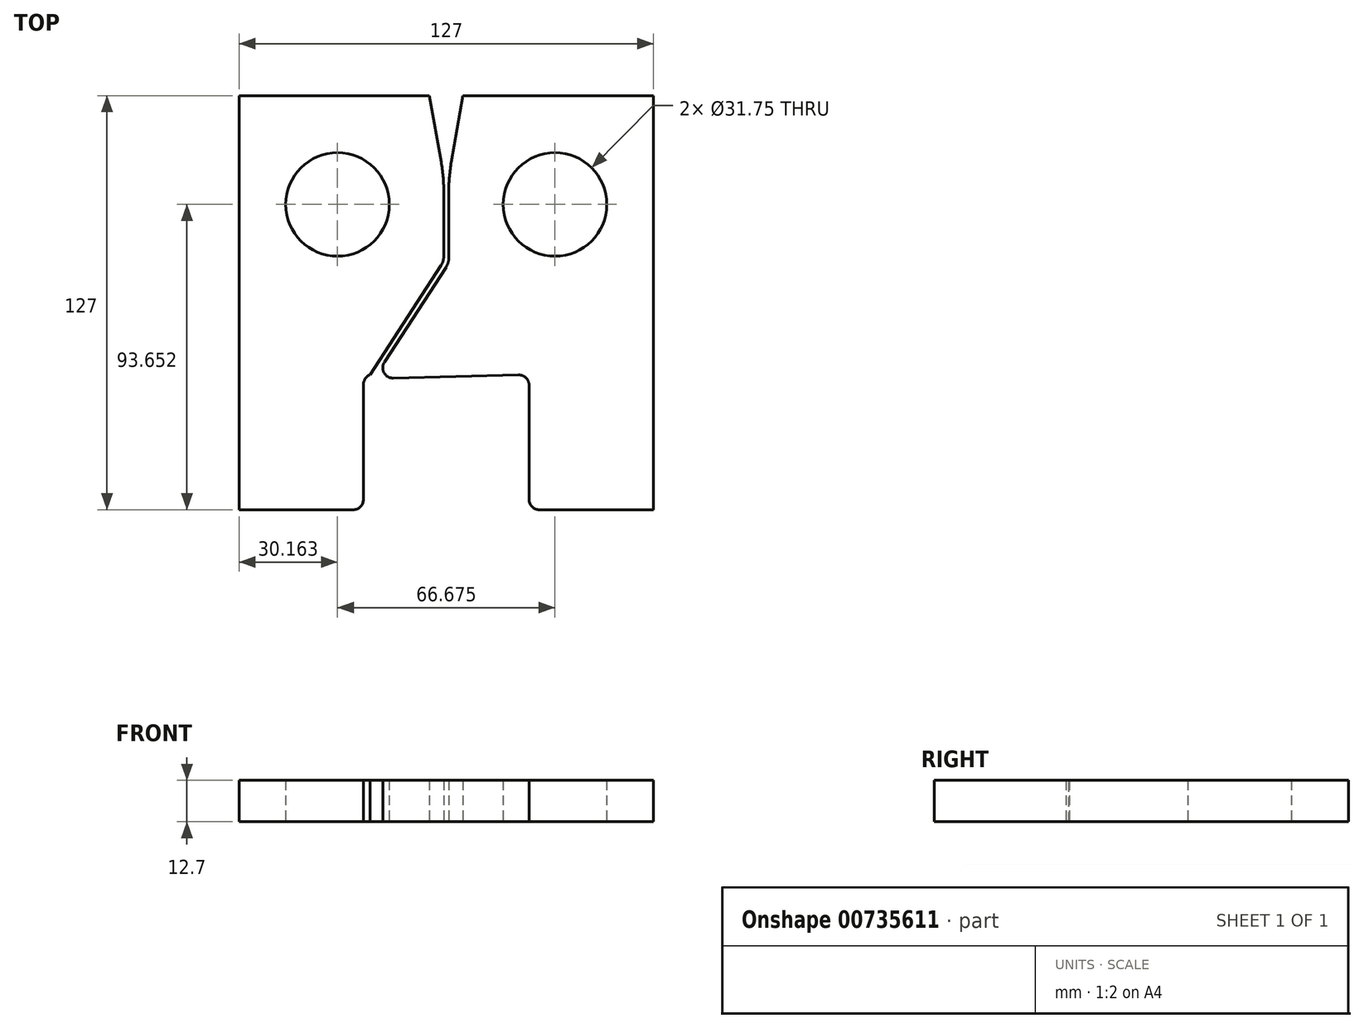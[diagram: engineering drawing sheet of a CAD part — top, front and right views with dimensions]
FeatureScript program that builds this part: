
annotation { "Feature Type Name" : "Feature", "Feature Type Description" : "" }
export const myFeature = defineFeature(function(context is Context, id is Id, definition is map)
    precondition{}
    {
        {
            var Q0;
            Q0=qCreatedBy(makeId("Top.planeOp"),FACE);
            var sketch = newSketch(context, id + "F0", { "sketchPlane" : qUnion([Q0])});
            skLineSegment(sketch, "E0.bottom", {"start": v(63.5, -63.5) * mm, "end": v(25.4, -63.5) * mm});
            skLineSegment(sketch, "E0.top", {"start": v(63.5, 63.5) * mm, "end": v(5.14, 63.5) * mm});
            skLineSegment(sketch, "E0.left", {"start": v(63.5, -63.5) * mm, "end": v(63.5, 63.5) * mm});
            skLineSegment(sketch, "E0.right", {"start": v(-63.5, -63.5) * mm, "end": v(-63.5, 63.5) * mm});
            skPoint(sketch, "E0.middle", {"position": v(0, 0) * mm});
            skLineSegment(sketch, "E1", {"start": v(-0.79, 38.8) * mm, "end": v(-0.79, 12.61) * mm});
            skLineSegment(sketch, "E2.MirrorCS", {"start": v(0.79, 38.8) * mm, "end": v(0.79, 12.18) * mm});
            skLineSegment(sketch, "E3.trimOffspring", {"start": v(-5.14, 63.5) * mm, "end": v(-63.5, 63.5) * mm});
            skLineSegment(sketch, "E4.trimOffspring", {"start": v(-25.4, -63.5) * mm, "end": v(-63.5, -63.5) * mm});
            skCircle(sketch, "E5", {"center": v(-33.34, 30.15) * mm, "radius": 15.88 * mm});
            skCircle(sketch, "E6.MirrorC", {"center": v(33.34, 30.15) * mm, "radius": 15.88 * mm});
            skLineSegment(sketch, "E7.left", {"start": v(25.4, -63.5) * mm, "end": v(25.4, -22.06) * mm});
            skLineSegment(sketch, "E7.right", {"start": v(-25.4, -63.5) * mm, "end": v(-25.4, -22.06) * mm});
            skPoint(sketch, "E7.middle", {"position": v(0, -63.34) * mm});
            skPoint(sketch, "E7.bottom.end.orphan", {"position": v(-25.4, -104.61) * mm});
            skPoint(sketch, "E7.bottom.start.orphan", {"position": v(25.4, -104.61) * mm});
            skPoint(sketch, "E8.orphan", {"position": v(-0.79, -63.5) * mm});
            skPoint(sketch, "E9.orphan", {"position": v(0.79, -63.5) * mm});
            skLineSegment(sketch, "E10", {"start": v(-23.31, -22.06) * mm, "end": v(-0.79, 12.61) * mm});
            skLineSegment(sketch, "E11", {"start": v(-21.46, -22.06) * mm, "end": v(0.79, 12.18) * mm});
            skLineSegment(sketch, "E12.trimOffspring", {"start": v(-23.31, -22.06) * mm, "end": v(-25.4, -22.06) * mm});
            skLineSegment(sketch, "E13", {"start": v(25.4, -22.06) * mm, "end": v(-22.24, -23.27) * mm});
            skLineSegment(sketch, "E14", {"start": v(0.79, 12.18) * mm, "end": v(-22.24, -23.27) * mm});
            skLineSegment(sketch, "E15", {"start": v(-0.79, 38.8) * mm, "end": v(-5.14, 63.5) * mm});
            skLineSegment(sketch, "E16.MirrorCS", {"start": v(0.79, 38.8) * mm, "end": v(5.14, 63.5) * mm});
            skPoint(sketch, "E17.orphan", {"position": v(-0.79, 63.5) * mm});
            skPoint(sketch, "E18.orphan", {"position": v(0.79, 63.5) * mm});
            skSolve(sketch);
        }
        {
            var Q0;
            Q0 = qSketchRegion(id + "F0", true);
            extrude(context, id + "F1", {"entities" : qUnion([Q0]), "depth" : 12.7 * mm, "offsetDistance" : 25.4 * mm});
        }
        {
            var Q0;
            Q0=makeQuery(id+"F1.opExtrude","SWEPT_EDGE",EDGE,{"disambiguationData":[OSD([sQuery(id+"F0.wireOp",EDGE,"E7.right"),sQuery(id+"F0.wireOp",EDGE,"77e37819-c0fe-4e0c-a129-227d0565c281.trimOffspring")])]});
            var Q1;
            Q1=makeQuery(id+"F1.opExtrude","SWEPT_EDGE",EDGE,{"disambiguationData":[OSD([sQuery(id+"F0.wireOp",EDGE,"E7.top"),sQuery(id+"F0.wireOp",EDGE,"E7.left")])]});
            fillet(context, id + "F2", {"entities" : qUnion([Q0, Q1]), "radius" : 3.17 * mm, "tangentPropagation" : true, "allowEdgeOverflow" : false});
        }
        {
            var Q0;
            Q0=makeQuery(id+"F1.opExtrude","SWEPT_EDGE",EDGE,{"disambiguationData":[OSD([sQuery(id+"F0.wireOp",EDGE,"E1"),sQuery(id+"F0.wireOp",EDGE,"E15")])]});
            var Q1;
            Q1=makeQuery(id+"F1.opExtrude","SWEPT_EDGE",EDGE,{"disambiguationData":[OSD([sQuery(id+"F0.wireOp",EDGE,"E2.MirrorCS"),sQuery(id+"F0.wireOp",EDGE,"E16.MirrorCS")])]});
            fillet(context, id + "F3", {"entities" : qUnion([Q0, Q1]), "radius" : 50.8 * mm, "tangentPropagation" : true, "allowEdgeOverflow" : false});
        }
        {
            var Q0;
            Q0=makeQuery(id+"F1.opExtrude","SWEPT_EDGE",EDGE,{"disambiguationData":[OSD([sQuery(id+"F0.wireOp",EDGE,"E13"),sQuery(id+"F0.wireOp",EDGE,"E14")])]});
            fillet(context, id + "F4", {"entities" : qUnion([Q0]), "radius" : 3.17 * mm, "tangentPropagation" : true, "allowEdgeOverflow" : false});
        }
        {
            var Q0;
            Q0=makeQuery(id+"F1.opExtrude","SWEPT_EDGE",EDGE,{"disambiguationData":[OSD([sQuery(id+"F0.wireOp",EDGE,"E1"),sQuery(id+"F0.wireOp",EDGE,"E10")])]});
            var Q1;
            Q1=makeQuery(id+"F1.opExtrude","SWEPT_EDGE",EDGE,{"disambiguationData":[OSD([sQuery(id+"F0.wireOp",EDGE,"E2.MirrorCS"),sQuery(id+"F0.wireOp",EDGE,"E14")])]});
            fillet(context, id + "F5", {"entities" : qUnion([Q0, Q1]), "radius" : 5.08 * mm, "tangentPropagation" : true, "allowEdgeOverflow" : false});
        }
    });
